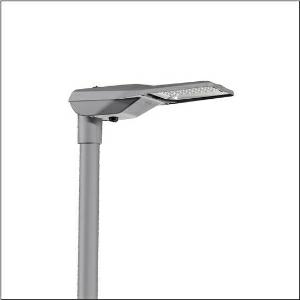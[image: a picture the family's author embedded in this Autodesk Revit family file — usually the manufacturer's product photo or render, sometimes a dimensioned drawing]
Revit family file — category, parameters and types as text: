
# Revit family: streetlight_sl_21_mini___p0_8ab_5xe2r33t08hb_4a65
name_source: partatom
category: Lighting Fixtures
units: mm (PartAtom-declared; Revit-internal decimal feet)

## family parameters
Cut with Voids When Loaded = No
Host = Face
Light Source = No
Part Type = Normal
Room Calculation Point = No
Round Connector Dimension = Use Diameter
Shared = No

## types (1)
- --- (1 x LED, 7850 lm, 66 W, 3000K)
    Apparent Load = 66 VA
    CIE Flux Codes = 36 71 98 100 100
    Color Rendering = 70
    Color Temperature = 3000K
    Default Elevation = 1800 mm
    Description = Streetlight SL 21 mini, mast luminaire, primary light control with lens, of PMMA, primary optical cover: cover, of toughened safety glass, transparent, light distribution: P0.8aB, light emission: direct distribution, primary light characteristic: asymmetric, installation type: post-top, side-entry, LED, High Power LED, rated luminous flux: 7.850lm, luminous efficacy: 119lm/W, light colour: 730, colour temperature: 3000K, control gear: D4i, control: pre-setting: logarithmic dimming characteristic, flexible luminous flux parameterisation, time-dependent luminous flux control, constant luminous flux control, overheat protection, mains connection: 220..240V, AC, 50/60Hz, start of lifetime: 66W, end of service life: 69W, reduction: 30W, luminaire housing, of diecast aluminium, powder-coated, SITECO metallic grey (DB 702S), corrosivity category C5 high according to DIN EN ISO 12944, multi-level sealing system, sealing non-destructively replaceable, inclination adjustable: 0°, 5°, 10°, 15°, please order mast flange separately, length: 628mm, width: 235mm, height: 110mm, mast flange for spigot size: 42mm (side-entry): 5XC10008XM4, 60/48mm (side-entry/post-top): 5XC10108XM2, 76/60mm (side-entry/post-top): 5XC10108XM1, mounting height: 4..8m, Smart Interface below and above, protection rating (complete): IP66, insulation class (complete): insulation class II (safety insulation), certification: CE, ENEC, ENEC+, VDE, impact resistance: IK10, permissible operating ambient temperature for outdoor applications: -40..+50°C, standard-compliant lighting for roads and squares, packaging unit: 1 piece

Light Distribution: P0.8aB
    Height = 110 mm
    Lamp = 1 x LED
    Lamp Light Flux = 7850 lm
    Lamp Power = 66 W
    Lamp count = 1
    Length = 625 mm
    Luminous efficacy = 119 lm/W
    Manufacturer = Siteco
    ModVariant = No
    Model = 5XE2R33T08HB
    Number of Poles = 1
    OnlyDefault = Yes
    Power Factor = 1
    Product Name = Streetlight SL 21 mini | P0.8aB
    Product group = mast luminaire | pylon top
    ProductGroupID = 6100
    Protection Class = Protection class II
    Protection Degree = IP 66
    RLX_Detail_Level = 1
    RLX_Emergency_Light_Flux = 0 lm
    RLX_Emergency_Type = 0
    RLX_Emergency_Type_DB = No
    RlxData = <blob elided: 91913 chars, md5=cd4a65bc>
    Socket = socket
    Standby Power = 0 W
    System Light Flux = 7850 lm
    System Power = 66 W
    Type Comments = factory setting: luminous flux: 100 % | dim-lin: 254 | 670 mA
    Type Image = l_1003514.jpg
    URL = http://relux.com
    VarID = @adj_082601
    Voltage = 0 V
    Weight = 0.00 kg
    Width = 234 mm

## geometry (parser evidence)
native form markers: Blend x4, Sweep x11
no freeform markers — native parametric forms only
